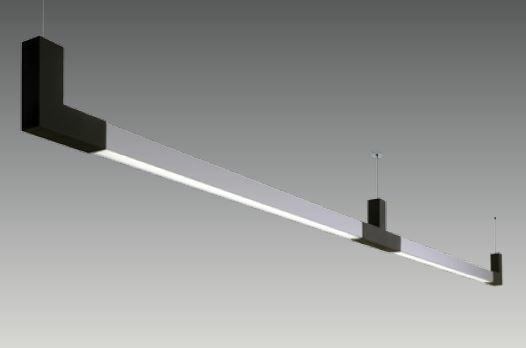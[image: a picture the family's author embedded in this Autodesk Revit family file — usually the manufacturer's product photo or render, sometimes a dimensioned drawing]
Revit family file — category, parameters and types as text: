
# Revit family: S 3500 PLT
name_source: partatom
category: Lighting Fixtures
revit_build: Autodesk Revit 2017 (Build: 20160225_1515(x64)
units: mm (PartAtom-declared; Revit-internal decimal feet)

## family parameters
Cut with Voids When Loaded = No
Host = Face
Light Source = Yes
Part Type = Normal
Room Calculation Point = No
Round Connector Dimension = Use Diameter
Shared = No

## types (2) — shared parameters
Color Filter = 16777215
Default Elevation = 1219 mm
Dimming Lamp Color Temperature Shift = <None>
Emit Shape Visible in Rendering = Yes
Emit from Rectangle Length = 40 mm  [stored 0.131234 ft]
Emit from Rectangle Width = 1400 mm  [stored 4.59318 ft]
Light Source Symbol Size = 610 mm
Manufacturer = ARLIGHT
Type Image = S 3500 PLT.JPG

## per-type parameters (varying)
| type | Wattage Comments |
| SDPLT.3500.108.30 | 108 |
| SDPLT.3500.108 .40 | 108W |

note: [stored X ft] marks values corroborated as IEEE doubles in the binary element streams (Revit-internal decimal feet)

## geometry (parser evidence)
native form markers: Sweep x3
no freeform markers — native parametric forms only
